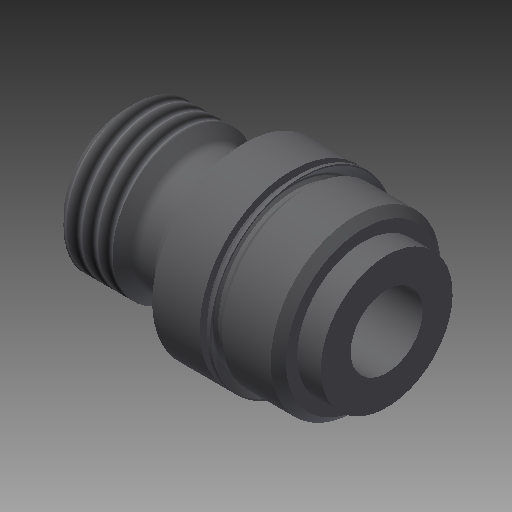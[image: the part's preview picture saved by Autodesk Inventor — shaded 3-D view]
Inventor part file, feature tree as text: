
AUTODESK INVENTOR PART (.ipt)
format: ipt  version: 2017 (Build 210142000, 142)  size: 287,232 bytes
history: native  units: in
note: dims shown in document units (in); Inventor stores cm internally (conversion verified against a paired STEP export)
features: other x112, sketch x5, revolve x4, thread x1, hole x1
ambient origin geometry x8: Origin, YZ Plane, XZ Plane, XY Plane, X Axis, Y Axis, Z Axis, Center Point
bodies: Solid1 (feature_tree)
feature tree (123):
  revolve  "Revolution1"  [1 undecoded]
  thread  "Thread1"  [1 undecoded]
  revolve  "Revolution2"  Angle=360.0deg
  revolve  "Revolution3"  [1 undecoded]
  hole  "Hole1"  [1 undecoded]
  revolve  "Revolution4"  [1 undecoded]
  other  "dp1_XY"
  other  "dp1_YZ"
  other  "dp1_ZX"
  other  "dp1_X"
  other  "dp1_Y"
  other  "dp1_Z"
  other  "dp1_Center"
  other  "dp2_XY"
  other  "dp2_YZ"
  other  "dp2_ZX"
  other  "dp2_X"
  other  "dp2_Y"
  other  "dp2_Z"
  other  "dp2_Center"
  other  "hh_XY"
  other  "hh_YZ"
  other  "hh_ZX"
  other  "hh_X"
  other  "hh_Y"
  other  "hh_Z"
  other  "hh_Center"
  other  "rod_guide_XY"
  other  "rod_guide_YZ"
  other  "rod_guide_ZX"
  other  "rod_guide_X"
  other  "rod_guide_Y"
  other  "rod_guide_Z"
  other  "rod_guide_Center"
  other  "s1_XY"
  other  "s1_YZ"
  other  "s1_ZX"
  other  "s1_X"
  other  "s1_Y"
  other  "s1_Z"
  other  "s1_Center"
  other  "s2_XY"
  other  "s2_YZ"
  other  "s2_ZX"
  other  "s2_X"
  other  "s2_Y"
  other  "s2_Z"
  other  "s2_Center"
  other  "t1_XY"
  other  "t1_YZ"
  other  "t1_ZX"
  other  "t1_X"
  other  "t1_Y"
  other  "t1_Z"
  other  "t1_Center"
  other  "t111_XY"
  other  "t111_YZ"
  other  "t111_ZX"
  other  "t111_X"
  other  "t111_Y"
  other  "t111_Z"
  other  "t111_Center"
  other  "to_foot_bracket_XY"
  other  "to_foot_bracket_YZ"
  other  "to_foot_bracket_ZX"
  other  "to_foot_bracket_X"
  other  "to_foot_bracket_Y"
  other  "to_foot_bracket_Z"
  other  "to_foot_bracket_Center"
  other  "to_nut_XY"
  other  "to_nut_YZ"
  other  "to_nut_ZX"
  other  "to_nut_X"
  other  "to_nut_Y"
  other  "to_nut_Z"
  other  "to_nut_Center"
  other  "to_rod_XY"
  other  "to_rod_YZ"
  other  "to_rod_ZX"
  other  "to_rod_X"
  other  "to_rod_Y"
  other  "to_rod_Z"
  other  "to_rod_Center"
  other  "to_screw_XY"
  other  "to_screw_YZ"
  other  "to_screw_ZX"
  other  "to_screw_X"
  other  "to_screw_Y"
  other  "to_screw_Z"
  other  "to_screw_Center"
  other  "to_trunnion_brackets_XY"
  other  "to_trunnion_brackets_YZ"
  other  "to_trunnion_brackets_ZX"
  other  "to_trunnion_brackets_X"
  other  "to_trunnion_brackets_Y"
  other  "to_trunnion_brackets_Z"
  other  "to_trunnion_brackets_Center"
  other  "to_trunnion_brackets1_XY"
  other  "to_trunnion_brackets1_YZ"
  other  "to_trunnion_brackets1_ZX"
  other  "to_trunnion_brackets1_X"
  other  "to_trunnion_brackets1_Y"
  other  "to_trunnion_brackets1_Z"
  other  "to_trunnion_brackets1_Center"
  other  "to_trunnion_brackets2_XY"
  other  "to_trunnion_brackets2_YZ"
  other  "to_trunnion_brackets2_ZX"
  other  "to_trunnion_brackets2_X"
  other  "to_trunnion_brackets2_Y"
  other  "to_trunnion_brackets2_Z"
  other  "to_trunnion_brackets2_Center"
  other  "to_tube_XY"
  other  "to_tube_YZ"
  other  "to_tube_ZX"
  other  "to_tube_X"
  other  "to_tube_Y"
  other  "to_tube_Z"
  other  "to_tube_Center"
  sketch  "Sketch_2"  dims[d0=360.0deg d1=0.1292in d2=0.0in d3=360.0deg]
  sketch  "Sketch_3"  dims[d4=360.0deg]
  sketch  "Sketch_4"  dims[d5=0.1895in d6=0.75in d7=0.2295in d8=0.25in d9=90.0deg d10=0.688in d11=0.0in d12=360.0deg]
  sketch  "Sketch4"  dims[d13=0.0in d14=0.0in d15=0.0in d16=0.0in d17=0.0in]
  sketch  "Sketch_47"
note: 5 required parameter values undecoded (feature->parameter linkage not recoverable at this tier; creation-order binding heuristic only, values carry confidence <= 0.55)